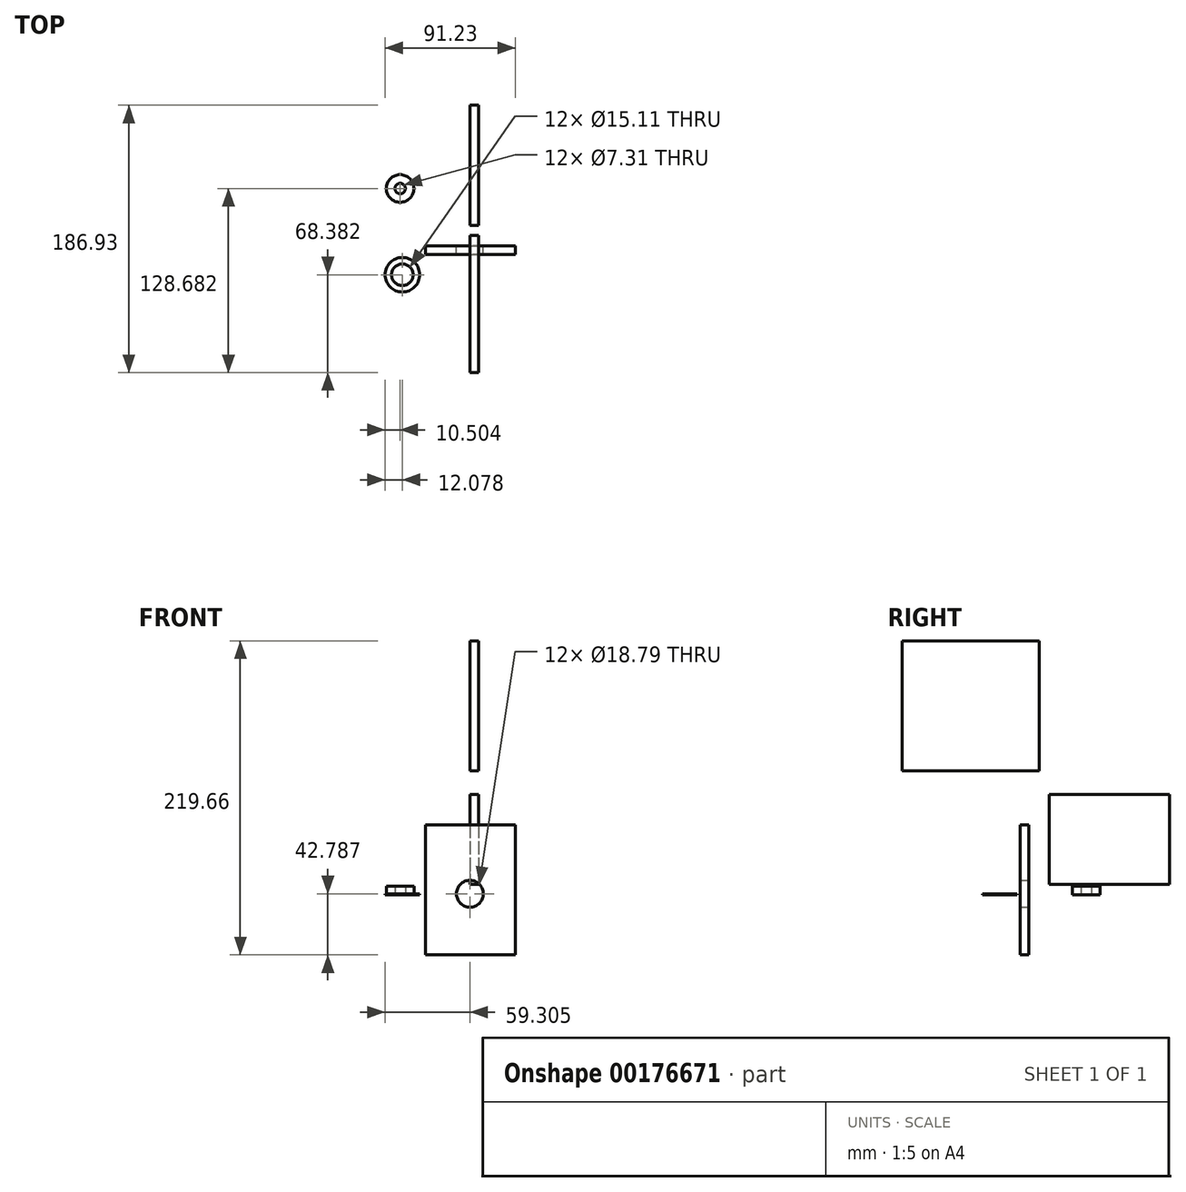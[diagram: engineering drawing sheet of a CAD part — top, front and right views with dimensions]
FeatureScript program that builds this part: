
annotation { "Feature Type Name" : "Feature", "Feature Type Description" : "" }
export const myFeature = defineFeature(function(context is Context, id is Id, definition is map)
    precondition{}
    {
        {
            var Q0;
            Q0=qCreatedBy(makeId("Front.planeOp"),FACE);
            var sketch = newSketch(context, id + "F0", { "sketchPlane" : qUnion([Q0])});
            skLineSegment(sketch, "E0.bottom", {"start": v(-31.08, 48.89) * mm, "end": v(31.92, 48.89) * mm});
            skLineSegment(sketch, "E0.top", {"start": v(-31.08, -42.11) * mm, "end": v(31.92, -42.11) * mm});
            skLineSegment(sketch, "E0.left", {"start": v(-31.08, 48.89) * mm, "end": v(-31.08, -42.11) * mm});
            skLineSegment(sketch, "E0.right", {"start": v(31.92, 48.89) * mm, "end": v(31.92, -42.11) * mm});
            skCircle(sketch, "E1", {"center": v(0, 0.68) * mm, "radius": 9.4 * mm});
            skSolve(sketch);
        }
        {
            var Q0;
            Q0=makeQuery(id+"F0.imprint","IMPRINT",FACE,{"disambiguationData":[TD([[makeQuery(id+"F0.imprint","IMPRINT",EDGE,{"derivedFrom":sQuery(id+"F0.wireOp",EDGE,"E0.bottom")}),-1.0]])]});
            extrude(context, id + "F1", {"entities" : qUnion([Q0]), "depth" : 6 * mm});
        }
        {
            var Q0;
            Q0=qCreatedBy(makeId("Right.planeOp"),FACE);
            var sketch = newSketch(context, id + "F2", { "sketchPlane" : qUnion([Q0])});
            skLineSegment(sketch, "E2.bottom", {"start": v(-88.6, 177.55) * mm, "end": v(7.4, 177.55) * mm});
            skLineSegment(sketch, "E2.top", {"start": v(-88.6, 86.55) * mm, "end": v(7.4, 86.55) * mm});
            skLineSegment(sketch, "E2.left", {"start": v(-88.6, 177.55) * mm, "end": v(-88.6, 86.55) * mm});
            skLineSegment(sketch, "E2.right", {"start": v(7.4, 177.55) * mm, "end": v(7.4, 86.55) * mm});
            skSolve(sketch);
        }
        {
            var Q0;
            Q0 = qSketchRegion(id + "F2", true);
            extrude(context, id + "F3", {"entities" : qUnion([Q0]), "operationType" : NewBodyOperationType.ADD, "depth" : 6 * mm});
        }
        {
            var Q0;
            Q0=qCreatedBy(makeId("Top.planeOp"),FACE);
            var sketch = newSketch(context, id + "F4", { "sketchPlane" : qUnion([Q0])});
            skCircle(sketch, "E3", {"center": v(-48.8, 40.08) * mm, "radius": 9.65 * mm});
            skCircle(sketch, "E4", {"center": v(-48.8, 40.08) * mm, "radius": 3.65 * mm});
            skSolve(sketch);
        }
        {
            var Q0;
            Q0 = qSketchRegion(id + "F4", true);
            extrude(context, id + "F5", {"entities" : qUnion([Q0]), "depth" : 6 * mm});
        }
        {
            var Q0;
            Q0=qCreatedBy(makeId("Right.planeOp"),FACE);
            var sketch = newSketch(context, id + "F6", { "sketchPlane" : qUnion([Q0])});
            skLineSegment(sketch, "E5.bottom", {"start": v(14.33, 70.08) * mm, "end": v(98.33, 70.08) * mm});
            skLineSegment(sketch, "E5.top", {"start": v(14.33, 7.08) * mm, "end": v(98.33, 7.08) * mm});
            skLineSegment(sketch, "E5.left", {"start": v(14.33, 70.08) * mm, "end": v(14.33, 7.08) * mm});
            skLineSegment(sketch, "E5.right", {"start": v(98.33, 70.08) * mm, "end": v(98.33, 7.08) * mm});
            skSolve(sketch);
        }
        {
            var Q0;
            Q0=makeQuery(id+"F6.imprint","IMPRINT",FACE,{"disambiguationData":[TD([[makeQuery(id+"F6.imprint","IMPRINT",EDGE,{"derivedFrom":sQuery(id+"F6.wireOp",EDGE,"E5.bottom")}),-1.0]])]});
            extrude(context, id + "F7", {"entities" : qUnion([Q0]), "depth" : 6 * mm});
        }
        {
            var Q0;
            Q0=qCreatedBy(makeId("Top.planeOp"),FACE);
            var sketch = newSketch(context, id + "F8", { "sketchPlane" : qUnion([Q0])});
            skCircle(sketch, "E6", {"center": v(-47.23, -20.22) * mm, "radius": 7.55 * mm});
            skCircle(sketch, "E7", {"center": v(-47.23, -20.22) * mm, "radius": 12.07 * mm});
            skSolve(sketch);
        }
        {
            var Q0;
            Q0=makeQuery(id+"F8.imprint","IMPRINT",FACE,{"disambiguationData":[TD([[makeQuery(id+"F8.imprint","IMPRINT",EDGE,{"derivedFrom":sQuery(id+"F8.wireOp",EDGE,"E6")}),-1.0]])]});
            var Q1;
            Q1=sQuery(id+"F8.wireOp",EDGE,"E6");
            var Q2;
            Q2=sQuery(id+"F8.wireOp",EDGE,"E7");
            extrude(context, id + "F9", {"entities" : qUnion([Q0]), "surfaceEntities" : qUnion([Q1, Q2]), "depth" : 0.5 * mm});
        }
    });
